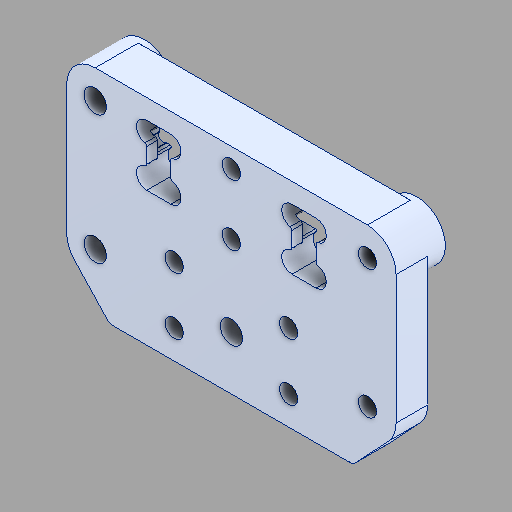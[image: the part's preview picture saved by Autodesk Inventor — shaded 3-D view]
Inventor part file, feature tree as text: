
AUTODESK INVENTOR PART (.ipt)
format: ipt  version: 2024.2 (Build 282272000, 272)  size: 228,352 bytes
history: native  units: in
note: dims shown in document units (in); Inventor stores cm internally (conversion verified against a paired STEP export)
features: fillet x1
ambient origin geometry x8: Origin, YZ Plane, XZ Plane, XY Plane, X Axis, Y Axis, Z Axis, Center Point
bodies: Solid1 (feature_tree)
feature tree (1):
  fillet  "Fillet10"  [1 undecoded]
note: 1 required parameter value undecoded (feature->parameter linkage not recoverable at this tier; creation-order binding heuristic only, values carry confidence <= 0.55)
